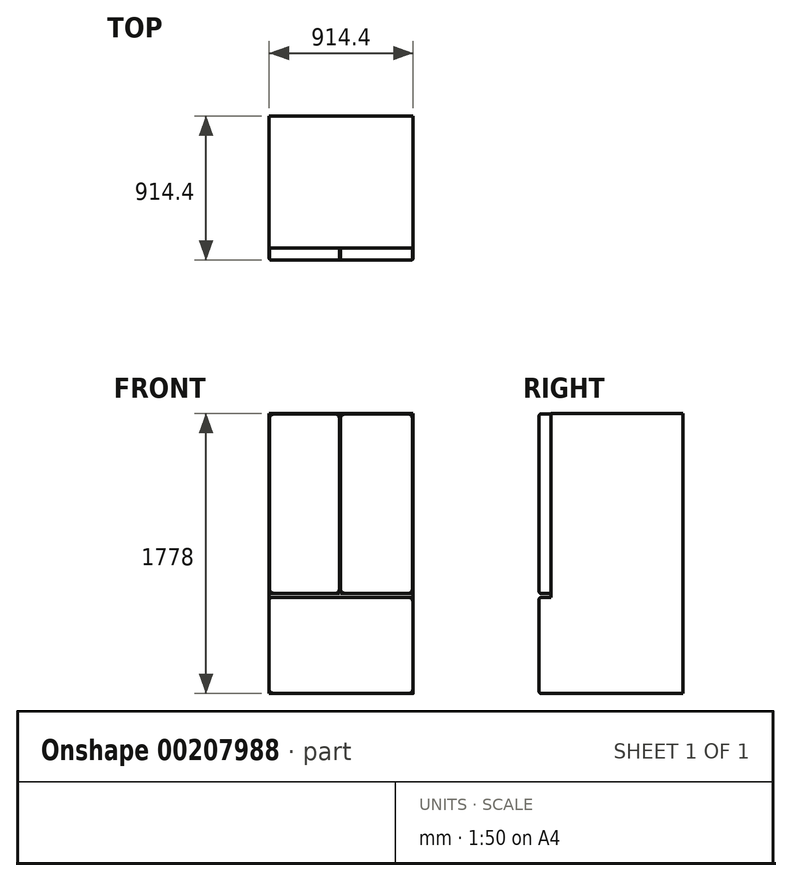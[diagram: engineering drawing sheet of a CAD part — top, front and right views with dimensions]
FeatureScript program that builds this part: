
annotation { "Feature Type Name" : "Feature", "Feature Type Description" : "" }
export const myFeature = defineFeature(function(context is Context, id is Id, definition is map)
    precondition{}
    {
        {
            var Q0;
            Q0=qCreatedBy(makeId("Top.planeOp"),FACE);
            var sketch = newSketch(context, id + "F0", { "sketchPlane" : qUnion([Q0])});
            skLineSegment(sketch, "E0.bottom", {"start": v(0, 0) * mm, "end": v(-914.4, 0) * mm});
            skLineSegment(sketch, "E0.top", {"start": v(0, -838.2) * mm, "end": v(-914.4, -838.2) * mm});
            skLineSegment(sketch, "E0.left", {"start": v(0, 0) * mm, "end": v(0, -838.2) * mm});
            skLineSegment(sketch, "E0.right", {"start": v(-914.4, 0) * mm, "end": v(-914.4, -838.2) * mm});
            skSolve(sketch);
        }
        {
            var Q0;
            Q0=makeQuery(id+"F0.imprint","IMPRINT",FACE,{"disambiguationData":[TD([[makeQuery(id+"F0.imprint","IMPRINT",EDGE,{"derivedFrom":sQuery(id+"F0.wireOp",EDGE,"E0.bottom")}),1.0]])]});
            extrude(context, id + "F1", {"entities" : qUnion([Q0]), "depth" : 1778 * mm});
        }
        {
            var Q0;
            Q0=makeQuery(id+"F1.opExtrude","SWEPT_FACE",FACE,{"disambiguationData":[OSD([sQuery(id+"F0.wireOp",EDGE,"E0.top")])]});
            var sketch = newSketch(context, id + "F2", { "sketchPlane" : qUnion([Q0])});
            skLineSegment(sketch, "E1.bottom", {"start": v(-914.4, 609.6) * mm, "end": v(0, 609.6) * mm});
            skLineSegment(sketch, "E1.top", {"start": v(-914.4, 0) * mm, "end": v(0, 0) * mm});
            skLineSegment(sketch, "E1.left", {"start": v(-914.4, 609.6) * mm, "end": v(-914.4, 0) * mm});
            skLineSegment(sketch, "E1.right", {"start": v(0, 609.6) * mm, "end": v(0, 0) * mm});
            skLineSegment(sketch, "E2.bottom", {"start": v(-911.86, 1775.46) * mm, "end": v(-466.1, 1775.46) * mm});
            skLineSegment(sketch, "E2.top", {"start": v(-911.86, 635) * mm, "end": v(-466.1, 635) * mm});
            skLineSegment(sketch, "E2.left", {"start": v(-911.86, 1775.46) * mm, "end": v(-911.86, 635) * mm});
            skLineSegment(sketch, "E2.right", {"start": v(-466.1, 1775.46) * mm, "end": v(-466.1, 635) * mm});
            skLineSegment(sketch, "E3.bottom", {"start": v(-459.74, 1775.46) * mm, "end": v(-2.54, 1775.46) * mm});
            skLineSegment(sketch, "E3.top", {"start": v(-459.74, 635) * mm, "end": v(-2.54, 635) * mm});
            skLineSegment(sketch, "E3.left", {"start": v(-459.74, 1775.46) * mm, "end": v(-459.74, 635) * mm});
            skLineSegment(sketch, "E3.right", {"start": v(-2.54, 1775.46) * mm, "end": v(-2.54, 635) * mm});
            skSolve(sketch);
        }
        {
            var Q0;
            Q0=makeQuery(id+"F2.imprint","IMPRINT",FACE,{"disambiguationData":[TD([[makeQuery(id+"F2.imprint","IMPRINT",EDGE,{"derivedFrom":sQuery(id+"F2.wireOp",EDGE,"E1.bottom")}),-1.0]])]});
            var Q1;
            Q1=makeQuery(id+"F2.imprint","IMPRINT",FACE,{"disambiguationData":[TD([[makeQuery(id+"F2.imprint","IMPRINT",EDGE,{"derivedFrom":sQuery(id+"F2.wireOp",EDGE,"E2.bottom")}),-1.0]])]});
            var Q2;
            Q2=makeQuery(id+"F2.imprint","IMPRINT",FACE,{"disambiguationData":[TD([[makeQuery(id+"F2.imprint","IMPRINT",EDGE,{"derivedFrom":sQuery(id+"F2.wireOp",EDGE,"E3.bottom")}),-1.0]])]});
            extrude(context, id + "F3", {"entities" : qUnion([Q0, Q1, Q2]), "operationType" : NewBodyOperationType.ADD, "depth" : 76.2 * mm});
        }
        {
            var Q0;
            Q0=makeQuery(id+"F3.opExtrude","CAP_EDGE",EDGE,{"disambiguationData":[OSD([sQuery(id+"F2.wireOp",EDGE,"E2.bottom")])],"isStart":false});
            var Q1;
            Q1=makeQuery(id+"F3.opExtrude","CAP_EDGE",EDGE,{"disambiguationData":[OSD([sQuery(id+"F2.wireOp",EDGE,"E2.right")])],"isStart":false});
            var Q2;
            Q2=makeQuery(id+"F3.opExtrude","CAP_EDGE",EDGE,{"disambiguationData":[OSD([sQuery(id+"F2.wireOp",EDGE,"E3.left")])],"isStart":false});
            var Q3;
            Q3=makeQuery(id+"F3.opExtrude","CAP_EDGE",EDGE,{"disambiguationData":[OSD([sQuery(id+"F2.wireOp",EDGE,"E3.bottom")])],"isStart":false});
            var Q4;
            Q4=makeQuery(id+"F3.opExtrude","CAP_EDGE",EDGE,{"disambiguationData":[OSD([sQuery(id+"F2.wireOp",EDGE,"E3.right")])],"isStart":false});
            var Q5;
            Q5=makeQuery(id+"F3.opExtrude","CAP_EDGE",EDGE,{"disambiguationData":[OSD([sQuery(id+"F2.wireOp",EDGE,"E3.top")])],"isStart":false});
            var Q6;
            Q6=makeQuery(id+"F3.opExtrude","CAP_EDGE",EDGE,{"disambiguationData":[OSD([sQuery(id+"F2.wireOp",EDGE,"E2.top")])],"isStart":false});
            var Q7;
            Q7=makeQuery(id+"F3.opExtrude","CAP_EDGE",EDGE,{"disambiguationData":[OSD([sQuery(id+"F2.wireOp",EDGE,"E2.left")])],"isStart":false});
            var Q8;
            Q8=makeQuery(id+"F3.opExtrude","CAP_EDGE",EDGE,{"disambiguationData":[OSD([sQuery(id+"F2.wireOp",EDGE,"E1.bottom")])],"isStart":false});
            var Q9;
            Q9=makeQuery(id+"F3.opExtrude","CAP_EDGE",EDGE,{"disambiguationData":[OSD([sQuery(id+"F2.wireOp",EDGE,"E1.left")])],"isStart":false});
            var Q10;
            Q10=makeQuery(id+"F3.opExtrude","CAP_EDGE",EDGE,{"disambiguationData":[OSD([sQuery(id+"F2.wireOp",EDGE,"E1.top")])],"isStart":false});
            var Q11;
            Q11=makeQuery(id+"F3.opExtrude","CAP_EDGE",EDGE,{"disambiguationData":[OSD([sQuery(id+"F2.wireOp",EDGE,"E1.right")])],"isStart":false});
            fillet(context, id + "F4", {"entities" : qUnion([Q0, Q1, Q2, Q3, Q4, Q5, Q6, Q7, Q8, Q9, Q10, Q11]), "radius" : 12.7 * mm, "tangentPropagation" : true, "allowEdgeOverflow" : false});
        }
    });
